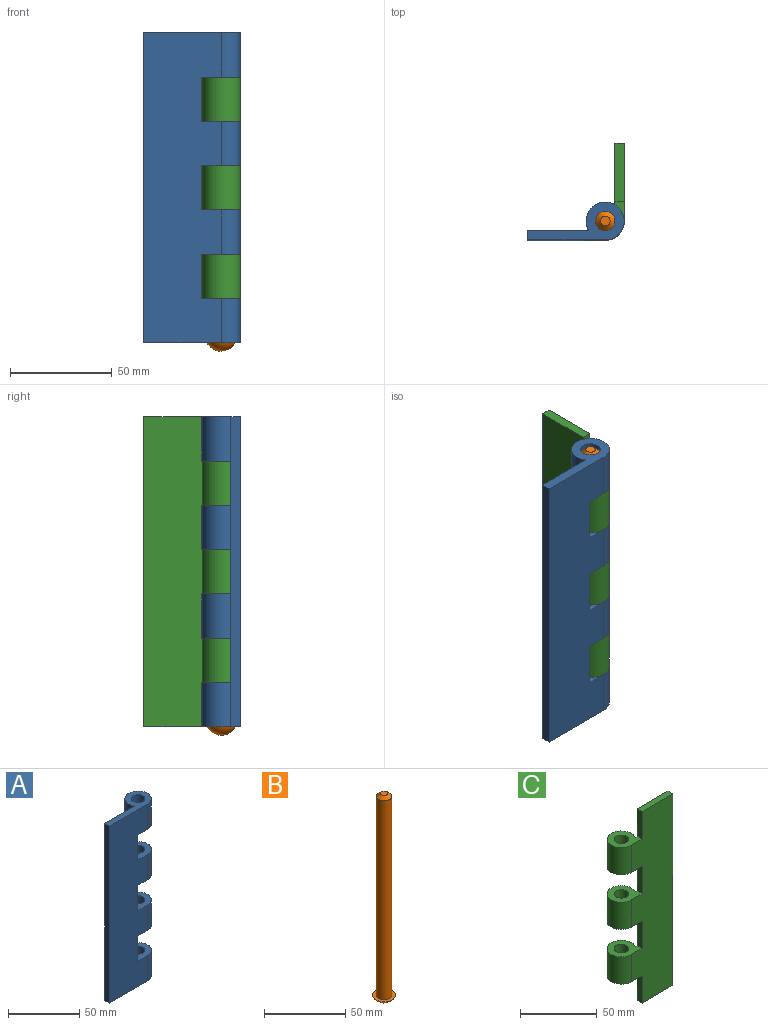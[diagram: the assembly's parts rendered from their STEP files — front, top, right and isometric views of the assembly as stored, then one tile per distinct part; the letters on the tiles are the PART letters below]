
ASSEMBLY  parts=3 mates=2
PART A: 22 faces, bbox 47.4x18.7x152.4 mm
  f0: plane 21.77x4.57mm, normal (1,0,0), area 99.5mm2, adj f4,f5,f18,f19
  f1: plane 21.77x4.57mm, normal (1,0,0), area 99.5mm2, adj f4,f5,f14,f16
  f2: plane 21.77x4.57mm, normal (1,0,0), area 99.5mm2, adj f4,f5,f10,f12
  f3: plane 152.4x4.57mm, normal (-1,0,0), area 696.8mm2, adj f4,f5,f6,f7
  f4: plane 152.4x38.1mm, normal (0,-1,0), area 5172.4mm2, adj f0,f1,f2,f3,f6,f7,f8,f10
  f5: plane 152.4x30.08mm, normal (0,1,0), area 4473.7mm2, adj f0,f1,f2,f3,f6,f7,f8,f10
  f6: plane 47.43x18.65mm, normal (0,0,1), area 350.2mm2, adj f3,f4,f5,f20,f21
  f7: plane 47.43x18.65mm, normal (0,0,-1), area 350.2mm2, adj f3,f4,f5,f8,f9
  f8: cylinder r=9.33mm len=21.77mm, axis (0,0,-1), area 1065.5mm2, adj f4,f5,f7,f10
  f9: cylinder r=4.76mm len=21.77mm, axis (0,0,-1), area 651.5mm2, adj f7,f10
  f10: plane 19.03x18.65mm, normal (0,0,1), area 220.4mm2, adj f2,f4,f5,f8,f9
  f11: cylinder r=9.33mm len=21.77mm, axis (0,0,-1), area 1065.5mm2, adj f4,f5,f12,f14
  f12: plane 19.03x18.65mm, normal (0,0,-1), area 220.4mm2, adj f2,f4,f5,f11,f13
  f13: cylinder r=4.76mm len=21.77mm, axis (0,0,-1), area 651.5mm2, adj f12,f14
  f14: plane 19.03x18.65mm, normal (0,0,1), area 220.4mm2, adj f1,f4,f5,f11,f13
  f15: cylinder r=9.33mm len=21.77mm, axis (0,0,-1), area 1065.5mm2, adj f4,f5,f16,f18
  f16: plane 19.03x18.65mm, normal (0,0,-1), area 220.4mm2, adj f1,f4,f5,f15,f17
  f17: cylinder r=4.76mm len=21.77mm, axis (0,0,-1), area 651.5mm2, adj f16,f18
  f18: plane 19.03x18.65mm, normal (0,0,1), area 220.4mm2, adj f0,f4,f5,f15,f17
  f19: plane 19.03x18.65mm, normal (0,0,-1), area 220.4mm2, adj f0,f4,f5,f20,f21
  f20: cylinder r=9.33mm len=21.77mm, axis (0,0,-1), area 1065.5mm2, adj f4,f5,f6,f19
  f21: cylinder r=4.76mm len=21.77mm, axis (0,0,-1), area 651.5mm2, adj f6,f19
PART B: 5 faces, bbox 14.1x14.1x156.5 mm
  f0: sphere r=8.09mm, area 209.1mm2, adj f2
  f1: cylinder r=4.76mm len=150.02mm, axis (0,0,-1), area 4489.1mm2, adj f2,f4
  f2: plane 14.09x14.09mm, normal (0,0,1), area 84.6mm2, adj f0,f1
  f3: plane 4.76x4.76mm, normal (0,0,1), area 17.8mm2, adj f4
  f4: cone r=2.38mm half-angle=45deg, axis (0,0,-1), area 75.6mm2, adj f1,f3
PART C: 21 faces, bbox 47.4x18.7x152.4 mm
  f0: cylinder r=9.33mm len=21.77mm, axis (0,0,-1), area 1065.5mm2, adj f7,f9,f18,f20
  f1: cylinder r=4.76mm len=21.77mm, axis (0,0,-1), area 651.5mm2, adj f15,f17
  f2: cylinder r=9.33mm len=21.77mm, axis (0,0,-1), area 1065.5mm2, adj f7,f9,f15,f17
  f3: cylinder r=4.76mm len=21.77mm, axis (0,0,-1), area 651.5mm2, adj f12,f14
  f4: plane 28.39x4.57mm, normal (0,0,1), area 129.8mm2, adj f6,f7,f9,f19
  f5: plane 28.39x4.57mm, normal (0,0,-1), area 129.8mm2, adj f6,f7,f9,f11
  f6: plane 152.4x4.57mm, normal (1,0,0), area 696.8mm2, adj f4,f5,f7,f9
  f7: plane 152.4x30.08mm, normal (0,1,0), area 4437mm2, adj f0,f2,f4,f5,f6,f8,f11,f12
  f8: cylinder r=9.33mm len=21.77mm, axis (0,0,-1), area 1065.5mm2, adj f7,f9,f12,f14
  f9: plane 152.4x38.1mm, normal (0,-1,0), area 4961mm2, adj f0,f2,f4,f5,f6,f8,f11,f12
  f10: cylinder r=4.76mm len=21.77mm, axis (0,0,-1), area 651.5mm2, adj f18,f20
  f11: plane 21.77x4.57mm, normal (-1,0,0), area 99.5mm2, adj f5,f7,f9,f12
  f12: plane 19.03x18.65mm, normal (0,0,-1), area 220.4mm2, adj f3,f7,f8,f9,f11
  f13: plane 21.77x4.57mm, normal (-1,0,0), area 99.5mm2, adj f7,f9,f14,f15
  f14: plane 19.03x18.65mm, normal (0,0,1), area 220.4mm2, adj f3,f7,f8,f9,f13
  f15: plane 19.03x18.65mm, normal (0,0,-1), area 220.4mm2, adj f1,f2,f7,f9,f13
  f16: plane 21.77x4.57mm, normal (-1,0,0), area 99.5mm2, adj f7,f9,f17,f18
  f17: plane 19.03x18.65mm, normal (0,0,1), area 220.4mm2, adj f1,f2,f7,f9,f16
  f18: plane 19.03x18.65mm, normal (0,0,-1), area 220.4mm2, adj f0,f7,f9,f10,f16
  f19: plane 21.77x4.57mm, normal (-1,0,0), area 99.5mm2, adj f4,f7,f9,f20
  f20: plane 19.03x18.65mm, normal (0,0,1), area 220.4mm2, adj f0,f7,f9,f10,f19
PLACE A at identity fixed
PLACE B at identity
PLACE C rot(axis=(0,0,1),90deg) t=(0,0,0)mm
MATE fastened A.f8 <-> B.f1  axis (0,0,-1) through (0,0,-76.2)mm
MATE cylindrical C.f0 <-> A.f8  axis (0,0,-1) through (0,0,54.43)mm
